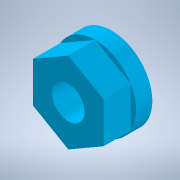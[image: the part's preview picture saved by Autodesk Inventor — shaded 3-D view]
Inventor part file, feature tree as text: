
AUTODESK INVENTOR PART (.ipt)
format: ipt  version: 2020 (Build 240168000, 168)  size: 138,240 bytes
history: native  units: mm
features: extrude x3, sketch x3, other x1
ambient origin geometry x8: Origin, YZ Plane, XZ Plane, XY Plane, X Axis, Y Axis, Z Axis, Center Point
bodies: Body1 (feature_tree)
feature tree (7):
  other  "ソリッド1"
  extrude  "押し出し1"  Depth=15.0mm
  extrude  "押し出し2"  Depth=3.0mm TaperAngle=0.0deg
  extrude  "押し出し3"  Depth=5.0mm TaperAngle=0.0deg
  sketch  "スケッチ1"
  sketch  "スケッチ2"
  sketch  "スケッチ3"
